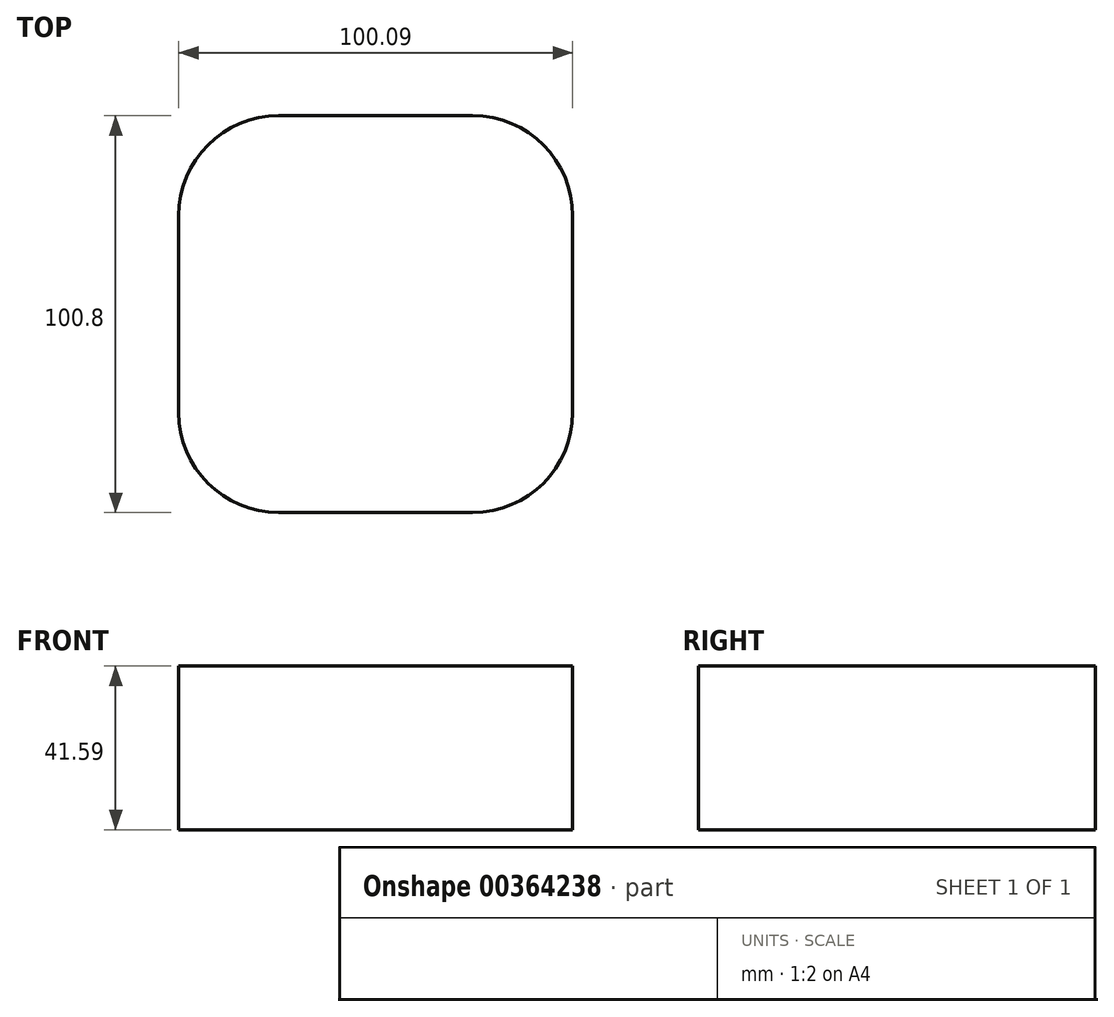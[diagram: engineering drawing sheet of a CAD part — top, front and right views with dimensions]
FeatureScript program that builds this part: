
annotation { "Feature Type Name" : "Feature", "Feature Type Description" : "" }
export const myFeature = defineFeature(function(context is Context, id is Id, definition is map)
    precondition{}
    {
        {
            var Q0;
            Q0=qCreatedBy(makeId("Top.planeOp"),FACE);
            var sketch = newSketch(context, id + "F0", { "sketchPlane" : qUnion([Q0])});
            skLineSegment(sketch, "E0.bottom", {"start": v(-19.33, 64.14) * mm, "end": v(29.96, 64.14) * mm});
            skLineSegment(sketch, "E0.top", {"start": v(-19.33, -36.66) * mm, "end": v(29.96, -36.66) * mm});
            skLineSegment(sketch, "E0.left", {"start": v(-44.73, 38.74) * mm, "end": v(-44.73, -11.26) * mm});
            skLineSegment(sketch, "E0.right", {"start": v(55.36, 38.74) * mm, "end": v(55.36, -11.26) * mm});
            skPoint(sketch, "E1.visualSharp", {"position": v(-44.73, 64.14) * mm});
            skArc(sketch, "E1.filletArc", {"start": v(-19.33, 64.14) * mm, "mid": v(-37.29, 56.7) * mm, "end": v(-44.73, 38.74) * mm});
            skPoint(sketch, "E2.visualSharp", {"position": v(55.36, 64.14) * mm});
            skArc(sketch, "E2.filletArc", {"start": v(55.36, 38.74) * mm, "mid": v(47.92, 56.7) * mm, "end": v(29.96, 64.14) * mm});
            skPoint(sketch, "E3.visualSharp", {"position": v(-44.73, -36.66) * mm});
            skArc(sketch, "E3.filletArc", {"start": v(-44.73, -11.26) * mm, "mid": v(-37.29, -29.22) * mm, "end": v(-19.33, -36.66) * mm});
            skPoint(sketch, "E4.visualSharp", {"position": v(55.36, -36.66) * mm});
            skArc(sketch, "E4.filletArc", {"start": v(29.96, -36.66) * mm, "mid": v(47.92, -29.22) * mm, "end": v(55.36, -11.26) * mm});
            skSolve(sketch);
        }
        {
            var Q0;
            Q0=makeQuery(id+"F0.imprint","IMPRINT",FACE,{"disambiguationData":[TD([[makeQuery(id+"F0.imprint","IMPRINT",EDGE,{"derivedFrom":sQuery(id+"F0.wireOp",EDGE,"E0.bottom")}),-1.0]])]});
            extrude(context, id + "F1", {"entities" : qUnion([Q0]), "oppositeDirection" : true, "depth" : 41.6 * mm});
        }
    });
